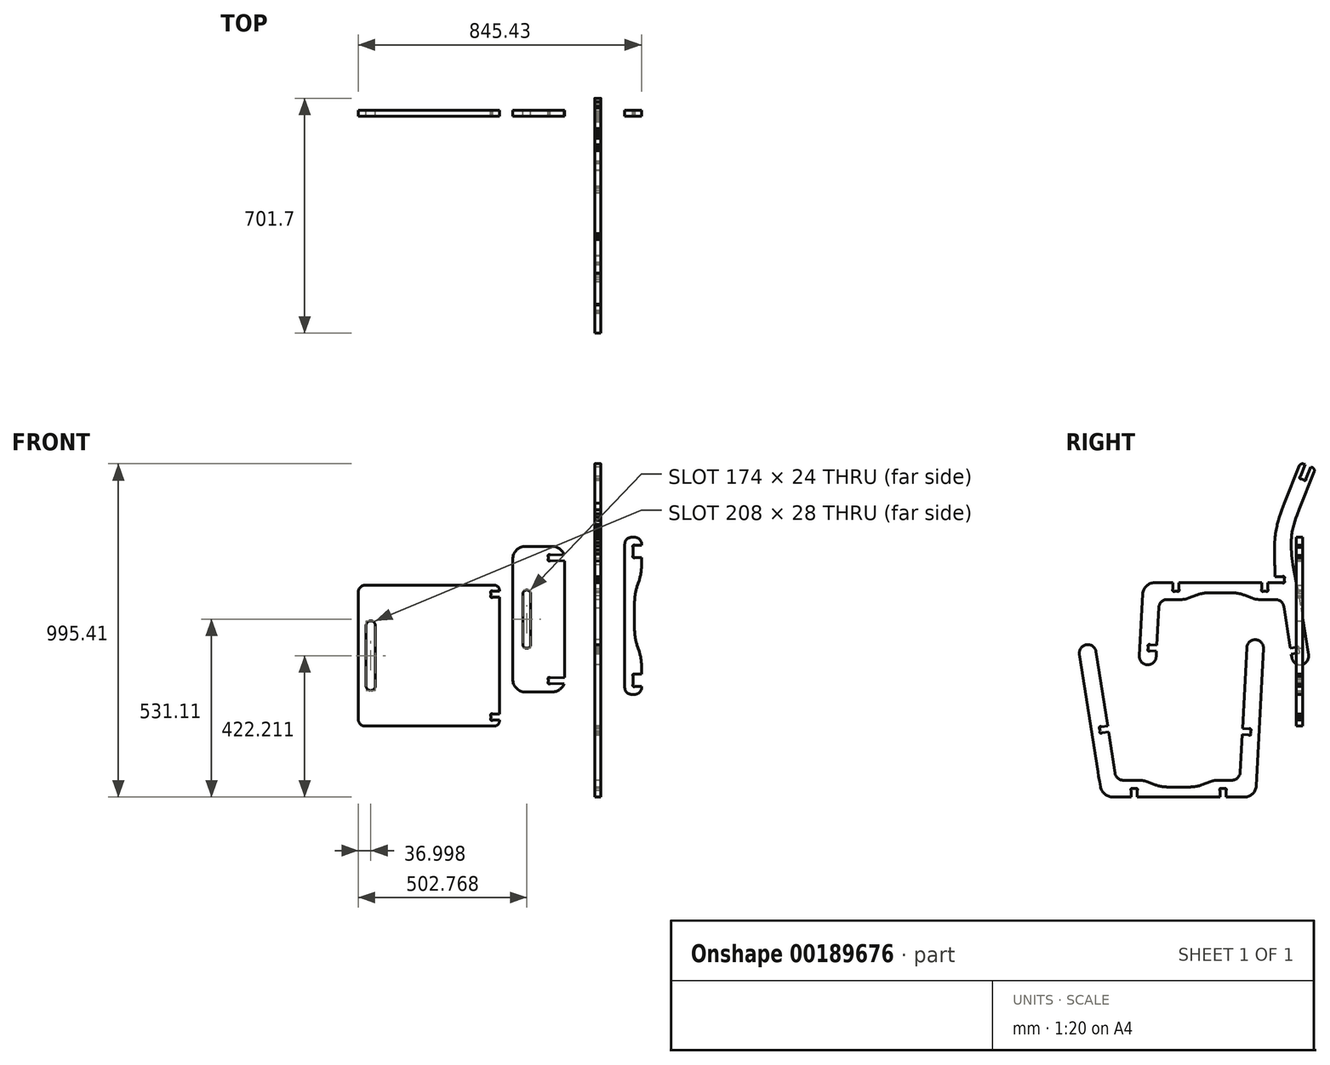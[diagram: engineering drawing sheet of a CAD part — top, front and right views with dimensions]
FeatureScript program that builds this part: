
annotation { "Feature Type Name" : "Feature", "Feature Type Description" : "" }
export const myFeature = defineFeature(function(context is Context, id is Id, definition is map)
    precondition{}
    {
        {
            assignVariable(context, id + "F0", {"name" : "ply", "anyValue" : 18});
        }
        {
            var Q0;
            Q0=qCreatedBy(makeId("Right.planeOp"),FACE);
            var sketch = newSketch(context, id + "F1", { "sketchPlane" : qUnion([Q0])});
            skLineSegment(sketch, "E0", {"start": v(-83.27, 173.83) * mm, "end": v(-83.93, 195.93) * mm});
            skLineSegment(sketch, "E1", {"start": v(-83.93, 195.93) * mm, "end": v(-83.96, 207) * mm});
            skLineSegment(sketch, "E2", {"start": v(-83.96, 207) * mm, "end": v(-83.75, 218.07) * mm});
            skLineSegment(sketch, "E3", {"start": v(-83.75, 218.07) * mm, "end": v(-83.24, 229.12) * mm});
            skLineSegment(sketch, "E4", {"start": v(-83.24, 229.12) * mm, "end": v(-82.4, 240.14) * mm});
            skLineSegment(sketch, "E5", {"start": v(-82.4, 240.14) * mm, "end": v(-81.86, 245.63) * mm});
            skLineSegment(sketch, "E6", {"start": v(-81.86, 245.63) * mm, "end": v(-81.2, 251.1) * mm});
            skLineSegment(sketch, "E7", {"start": v(-81.2, 251.1) * mm, "end": v(-80.46, 256.57) * mm});
            skLineSegment(sketch, "E8", {"start": v(-80.46, 256.57) * mm, "end": v(-79.6, 262.02) * mm});
            skLineSegment(sketch, "E9", {"start": v(-79.6, 262.02) * mm, "end": v(-78.64, 267.44) * mm});
            skLineSegment(sketch, "E10", {"start": v(-78.64, 267.44) * mm, "end": v(-77.57, 272.85) * mm});
            skLineSegment(sketch, "E11", {"start": v(-77.57, 272.85) * mm, "end": v(-76.4, 278.24) * mm});
            skLineSegment(sketch, "E12", {"start": v(-76.4, 278.24) * mm, "end": v(-75.13, 283.61) * mm});
            skLineSegment(sketch, "E13", {"start": v(-75.13, 283.61) * mm, "end": v(-72.33, 294.3) * mm});
            skLineSegment(sketch, "E14", {"start": v(-72.33, 294.3) * mm, "end": v(-69.21, 304.9) * mm});
            skLineSegment(sketch, "E15", {"start": v(-69.21, 304.9) * mm, "end": v(-65.8, 315.43) * mm});
            skLineSegment(sketch, "E16", {"start": v(-65.8, 315.43) * mm, "end": v(-62.16, 325.88) * mm});
            skLineSegment(sketch, "E17", {"start": v(-62.16, 325.88) * mm, "end": v(-54.3, 346.54) * mm});
            skLineSegment(sketch, "E18", {"start": v(-54.3, 346.54) * mm, "end": v(-9.72, 458.01) * mm});
            skArc(sketch, "E19", {"start": v(-9.72, 458.01) * mm, "mid": v(-4.37, 463.5) * mm, "end": v(3.28, 463.59) * mm});
            skLineSegment(sketch, "E20", {"start": v(3.28, 463.59) * mm, "end": v(7.92, 461.73) * mm});
            skLineSegment(sketch, "E21", {"start": v(7.92, 461.73) * mm, "end": v(-6.2, 426.41) * mm});
            skArc(sketch, "E22", {"start": v(-6.2, 426.41) * mm, "mid": v(-8.3, 421.16) * mm, "end": v(-3.05, 419.06) * mm});
            skLineSegment(sketch, "E23", {"start": v(-3.05, 419.06) * mm, "end": v(3.16, 416.58) * mm});
            skArc(sketch, "E24", {"start": v(3.16, 416.58) * mm, "mid": v(8.41, 414.48) * mm, "end": v(10.51, 419.73) * mm});
            skLineSegment(sketch, "E25", {"start": v(10.51, 419.73) * mm, "end": v(24.64, 455.04) * mm});
            skLineSegment(sketch, "E26", {"start": v(24.64, 455.04) * mm, "end": v(29.28, 453.19) * mm});
            skArc(sketch, "E27", {"start": v(29.28, 453.19) * mm, "mid": v(34.76, 447.84) * mm, "end": v(34.85, 440.19) * mm});
            skLineSegment(sketch, "E28", {"start": v(34.85, 440.19) * mm, "end": v(-9.74, 328.71) * mm});
            skLineSegment(sketch, "E29", {"start": v(-9.74, 328.71) * mm, "end": v(-16.51, 311.1) * mm});
            skLineSegment(sketch, "E30", {"start": v(-16.51, 311.1) * mm, "end": v(-19.69, 302.2) * mm});
            skLineSegment(sketch, "E31", {"start": v(-19.69, 302.2) * mm, "end": v(-22.66, 293.24) * mm});
            skLineSegment(sketch, "E32", {"start": v(-22.66, 293.24) * mm, "end": v(-25.37, 284.2) * mm});
            skLineSegment(sketch, "E33", {"start": v(-25.37, 284.2) * mm, "end": v(-26.61, 279.66) * mm});
            skLineSegment(sketch, "E34", {"start": v(-26.61, 279.66) * mm, "end": v(-27.77, 275.1) * mm});
            skLineSegment(sketch, "E35", {"start": v(-27.77, 275.1) * mm, "end": v(-28.85, 270.53) * mm});
            skLineSegment(sketch, "E36", {"start": v(-28.85, 270.53) * mm, "end": v(-29.83, 265.93) * mm});
            skLineSegment(sketch, "E37", {"start": v(-29.83, 265.93) * mm, "end": v(-30.7, 261.32) * mm});
            skLineSegment(sketch, "E38", {"start": v(-30.7, 261.32) * mm, "end": v(-31.48, 256.7) * mm});
            skLineSegment(sketch, "E39", {"start": v(-31.48, 256.7) * mm, "end": v(-32.14, 252.05) * mm});
            skLineSegment(sketch, "E40", {"start": v(-32.14, 252.05) * mm, "end": v(-32.69, 247.4) * mm});
            skLineSegment(sketch, "E41", {"start": v(-32.69, 247.4) * mm, "end": v(-33.13, 242.72) * mm});
            skLineSegment(sketch, "E42", {"start": v(-33.13, 242.72) * mm, "end": v(-33.48, 238.04) * mm});
            skLineSegment(sketch, "E43", {"start": v(-33.48, 238.04) * mm, "end": v(-33.72, 233.34) * mm});
            skLineSegment(sketch, "E44", {"start": v(-33.72, 233.34) * mm, "end": v(-33.88, 228.64) * mm});
            skLineSegment(sketch, "E45", {"start": v(-33.88, 228.64) * mm, "end": v(-33.94, 223.93) * mm});
            skLineSegment(sketch, "E46", {"start": v(-33.94, 223.93) * mm, "end": v(-33.92, 219.21) * mm});
            skLineSegment(sketch, "E47", {"start": v(-33.92, 219.21) * mm, "end": v(-33.63, 209.78) * mm});
            skLineSegment(sketch, "E48", {"start": v(-33.63, 209.78) * mm, "end": v(-33.04, 200.34) * mm});
            skLineSegment(sketch, "E49", {"start": v(-33.04, 200.34) * mm, "end": v(-32.18, 190.92) * mm});
            skLineSegment(sketch, "E50", {"start": v(-32.18, 190.92) * mm, "end": v(-31.1, 181.53) * mm});
            skLineSegment(sketch, "E51", {"start": v(-31.1, 181.53) * mm, "end": v(-29.8, 172.18) * mm});
            skLineSegment(sketch, "E52", {"start": v(-29.8, 172.18) * mm, "end": v(-28.33, 162.86) * mm});
            skLineSegment(sketch, "E53", {"start": v(-28.33, 162.86) * mm, "end": v(-10.62, 70.3) * mm});
            skLineSegment(sketch, "E54", {"start": v(-10.62, 70.3) * mm, "end": v(-4.36, 33.1) * mm});
            skLineSegment(sketch, "E55", {"start": v(-4.36, 33.1) * mm, "end": v(17.66, -107.27) * mm});
            skArc(sketch, "E56", {"start": v(17.66, -107.27) * mm, "mid": v(-3.16, -135.84) * mm, "end": v(-31.73, -115.02) * mm});
            skLineSegment(sketch, "E57", {"start": v(-31.73, -115.02) * mm, "end": v(-33.46, -104) * mm});
            skLineSegment(sketch, "E58", {"start": v(-33.46, -104) * mm, "end": v(-14.35, -101) * mm});
            skArc(sketch, "E59", {"start": v(-14.35, -101) * mm, "mid": v(-8.76, -100.13) * mm, "end": v(-9.64, -94.54) * mm});
            skLineSegment(sketch, "E60", {"start": v(-9.64, -94.54) * mm, "end": v(-10.68, -87.93) * mm});
            skArc(sketch, "E61", {"start": v(-10.68, -87.93) * mm, "mid": v(-11.55, -82.35) * mm, "end": v(-17.14, -83.22) * mm});
            skLineSegment(sketch, "E62", {"start": v(-17.14, -83.22) * mm, "end": v(-36.25, -86.22) * mm});
            skLineSegment(sketch, "E63", {"start": v(-36.25, -86.22) * mm, "end": v(-55.7, 37.73) * mm});
            skArc(sketch, "E64", {"start": v(-55.7, 37.73) * mm, "mid": v(-64.15, 52.85) * mm, "end": v(-80.4, 58.86) * mm});
            skLineSegment(sketch, "E65", {"start": v(-80.4, 58.86) * mm, "end": v(-128.9, 58.86) * mm});
            skArc(sketch, "E66", {"start": v(-128.9, 58.86) * mm, "mid": v(-139.97, 59.88) * mm, "end": v(-150.65, 62.94) * mm});
            skLineSegment(sketch, "E67", {"start": v(-150.65, 62.94) * mm, "end": v(-174.1, 72.06) * mm});
            skArc(sketch, "E68", {"start": v(-174.1, 72.06) * mm, "mid": v(-191.91, 77.14) * mm, "end": v(-210.35, 78.86) * mm});
            skLineSegment(sketch, "E69", {"start": v(-210.35, 78.86) * mm, "end": v(-279.97, 78.86) * mm});
            skArc(sketch, "E70", {"start": v(-279.97, 78.86) * mm, "mid": v(-298.41, 77.14) * mm, "end": v(-316.22, 72.06) * mm});
            skLineSegment(sketch, "E71", {"start": v(-316.22, 72.06) * mm, "end": v(-339.67, 62.94) * mm});
            skArc(sketch, "E72", {"start": v(-339.67, 62.94) * mm, "mid": v(-350.35, 59.88) * mm, "end": v(-361.42, 58.86) * mm});
            skLineSegment(sketch, "E73", {"start": v(-361.42, 58.86) * mm, "end": v(-404.15, 58.86) * mm});
            skArc(sketch, "E74", {"start": v(-404.15, 58.86) * mm, "mid": v(-421.35, 52) * mm, "end": v(-429.12, 35.18) * mm});
            skLineSegment(sketch, "E75", {"start": v(-429.12, 35.18) * mm, "end": v(-435.09, -77.5) * mm});
            skLineSegment(sketch, "E76", {"start": v(-435.09, -77.5) * mm, "end": v(-454.4, -76.47) * mm});
            skArc(sketch, "E77", {"start": v(-454.4, -76.47) * mm, "mid": v(-460.05, -76.17) * mm, "end": v(-460.35, -81.82) * mm});
            skLineSegment(sketch, "E78", {"start": v(-460.35, -81.82) * mm, "end": v(-460.7, -88.5) * mm});
            skArc(sketch, "E79", {"start": v(-460.7, -88.5) * mm, "mid": v(-461, -94.14) * mm, "end": v(-455.36, -94.44) * mm});
            skLineSegment(sketch, "E80", {"start": v(-455.36, -94.44) * mm, "end": v(-436.04, -95.47) * mm});
            skLineSegment(sketch, "E81", {"start": v(-436.04, -95.47) * mm, "end": v(-436.94, -112.47) * mm});
            skArc(sketch, "E82", {"start": v(-436.94, -112.47) * mm, "mid": v(-463.23, -136.1) * mm, "end": v(-486.87, -109.82) * mm});
            skLineSegment(sketch, "E83", {"start": v(-486.87, -109.82) * mm, "end": v(-477.04, 75.7) * mm});
            skArc(sketch, "E84", {"start": v(-477.04, 75.7) * mm, "mid": v(-466.17, 99.25) * mm, "end": v(-442.09, 108.86) * mm});
            skLineSegment(sketch, "E85", {"start": v(-442.09, 108.86) * mm, "end": v(-386.75, 108.86) * mm});
            skLineSegment(sketch, "E86", {"start": v(-386.75, 108.86) * mm, "end": v(-386.75, 89.51) * mm});
            skArc(sketch, "E87", {"start": v(-386.75, 89.51) * mm, "mid": v(-386.75, 83.86) * mm, "end": v(-381.1, 83.86) * mm});
            skLineSegment(sketch, "E88", {"start": v(-381.1, 83.86) * mm, "end": v(-374.4, 83.86) * mm});
            skArc(sketch, "E89", {"start": v(-374.4, 83.86) * mm, "mid": v(-368.75, 83.86) * mm, "end": v(-368.75, 89.51) * mm});
            skLineSegment(sketch, "E90", {"start": v(-368.75, 89.51) * mm, "end": v(-368.75, 108.86) * mm});
            skLineSegment(sketch, "E91", {"start": v(-368.75, 108.86) * mm, "end": v(-121.57, 108.86) * mm});
            skLineSegment(sketch, "E92", {"start": v(-121.57, 108.86) * mm, "end": v(-121.57, 89.51) * mm});
            skArc(sketch, "E93", {"start": v(-121.57, 89.51) * mm, "mid": v(-121.57, 83.86) * mm, "end": v(-115.92, 83.86) * mm});
            skLineSegment(sketch, "E94", {"start": v(-115.92, 83.86) * mm, "end": v(-109.23, 83.86) * mm});
            skArc(sketch, "E95", {"start": v(-109.23, 83.86) * mm, "mid": v(-103.57, 83.86) * mm, "end": v(-103.57, 89.51) * mm});
            skLineSegment(sketch, "E96", {"start": v(-103.57, 89.51) * mm, "end": v(-103.57, 108.86) * mm});
            skLineSegment(sketch, "E97", {"start": v(-103.57, 108.86) * mm, "end": v(-60.18, 108.86) * mm});
            skArc(sketch, "E98", {"start": v(-60.18, 108.86) * mm, "mid": v(-54.52, 108.86) * mm, "end": v(-54.52, 114.51) * mm});
            skLineSegment(sketch, "E99", {"start": v(-54.52, 114.51) * mm, "end": v(-54.52, 121.2) * mm});
            skArc(sketch, "E100", {"start": v(-54.52, 121.2) * mm, "mid": v(-54.52, 126.86) * mm, "end": v(-60.18, 126.86) * mm});
            skLineSegment(sketch, "E101", {"start": v(-60.18, 126.86) * mm, "end": v(-81.89, 126.86) * mm});
            skArc(sketch, "E102", {"start": v(-81.89, 126.86) * mm, "mid": v(-82.36, 150.35) * mm, "end": v(-83.27, 173.83) * mm});
            skSolve(sketch);
        }
        {
            var Q0;
            Q0 = qSketchRegion(id + "F1", true);
            extrude(context, id + "F2", {"entities" : qUnion([Q0]), "depth" : (getVariable(context, 'ply')) * mm});
        }
        {
            var Q0;
            Q0=qCreatedBy(makeId("Right.planeOp"),FACE);
            var sketch = newSketch(context, id + "F3", { "sketchPlane" : qUnion([Q0])});
            skArc(sketch, "E103", {"start": v(-211.02, -481.11) * mm, "mid": v(-193.81, -474.25) * mm, "end": v(-186.05, -457.44) * mm});
            skLineSegment(sketch, "E104", {"start": v(-186.05, -457.44) * mm, "end": v(-180.08, -344.77) * mm});
            skLineSegment(sketch, "E105", {"start": v(-180.08, -344.77) * mm, "end": v(-160.76, -345.8) * mm});
            skArc(sketch, "E106", {"start": v(-160.76, -345.8) * mm, "mid": v(-155.11, -346.09) * mm, "end": v(-154.81, -340.44) * mm});
            skLineSegment(sketch, "E107", {"start": v(-154.81, -340.44) * mm, "end": v(-154.48, -334.06) * mm});
            skArc(sketch, "E108", {"start": v(-154.48, -334.06) * mm, "mid": v(-153.88, -328.43) * mm, "end": v(-159.5, -327.83) * mm});
            skLineSegment(sketch, "E109", {"start": v(-159.5, -327.83) * mm, "end": v(-179.13, -326.8) * mm});
            skLineSegment(sketch, "E110", {"start": v(-179.13, -326.8) * mm, "end": v(-166.3, -84.76) * mm});
            skArc(sketch, "E111", {"start": v(-166.3, -84.76) * mm, "mid": v(-140, -61.11) * mm, "end": v(-116.37, -87.4) * mm});
            skLineSegment(sketch, "E112", {"start": v(-116.37, -87.4) * mm, "end": v(-138.13, -497.97) * mm});
            skArc(sketch, "E113", {"start": v(-138.13, -497.97) * mm, "mid": v(-149, -521.5) * mm, "end": v(-173.08, -531.11) * mm});
            skLineSegment(sketch, "E114", {"start": v(-173.08, -531.11) * mm, "end": v(-228.42, -531.11) * mm});
            skLineSegment(sketch, "E115", {"start": v(-228.42, -531.11) * mm, "end": v(-228.42, -511.77) * mm});
            skArc(sketch, "E116", {"start": v(-228.42, -511.77) * mm, "mid": v(-228.42, -506.11) * mm, "end": v(-234.08, -506.11) * mm});
            skLineSegment(sketch, "E117", {"start": v(-234.08, -506.11) * mm, "end": v(-240.76, -506.11) * mm});
            skArc(sketch, "E118", {"start": v(-240.76, -506.11) * mm, "mid": v(-246.42, -506.11) * mm, "end": v(-246.42, -511.77) * mm});
            skLineSegment(sketch, "E119", {"start": v(-246.42, -511.77) * mm, "end": v(-246.42, -531.11) * mm});
            skLineSegment(sketch, "E120", {"start": v(-246.42, -531.11) * mm, "end": v(-493.6, -531.11) * mm});
            skLineSegment(sketch, "E121", {"start": v(-493.6, -531.11) * mm, "end": v(-493.6, -511.77) * mm});
            skArc(sketch, "E122", {"start": v(-493.6, -511.77) * mm, "mid": v(-493.6, -506.11) * mm, "end": v(-499.25, -506.11) * mm});
            skLineSegment(sketch, "E123", {"start": v(-499.25, -506.11) * mm, "end": v(-505.94, -506.11) * mm});
            skArc(sketch, "E124", {"start": v(-505.94, -506.11) * mm, "mid": v(-511.6, -506.11) * mm, "end": v(-511.6, -511.77) * mm});
            skLineSegment(sketch, "E125", {"start": v(-511.6, -511.77) * mm, "end": v(-511.6, -531.11) * mm});
            skLineSegment(sketch, "E126", {"start": v(-511.6, -531.11) * mm, "end": v(-565.95, -531.11) * mm});
            skArc(sketch, "E127", {"start": v(-565.95, -531.11) * mm, "mid": v(-590.26, -522.32) * mm, "end": v(-603.32, -500) * mm});
            skLineSegment(sketch, "E128", {"start": v(-603.32, -500) * mm, "end": v(-604.68, -492.5) * mm});
            skLineSegment(sketch, "E129", {"start": v(-604.68, -492.5) * mm, "end": v(-605.99, -485.03) * mm});
            skLineSegment(sketch, "E130", {"start": v(-605.99, -485.03) * mm, "end": v(-607.65, -475.1) * mm});
            skLineSegment(sketch, "E131", {"start": v(-607.65, -475.1) * mm, "end": v(-608.72, -468.52) * mm});
            skLineSegment(sketch, "E132", {"start": v(-608.72, -468.52) * mm, "end": v(-610.8, -455.37) * mm});
            skLineSegment(sketch, "E133", {"start": v(-610.8, -455.37) * mm, "end": v(-665.83, -104.69) * mm});
            skArc(sketch, "E134", {"start": v(-665.83, -104.69) * mm, "mid": v(-645, -76.11) * mm, "end": v(-616.43, -96.94) * mm});
            skLineSegment(sketch, "E135", {"start": v(-616.43, -96.94) * mm, "end": v(-581.7, -318.25) * mm});
            skLineSegment(sketch, "E136", {"start": v(-581.7, -318.25) * mm, "end": v(-600.82, -321.25) * mm});
            skArc(sketch, "E137", {"start": v(-600.82, -321.25) * mm, "mid": v(-606.4, -322.13) * mm, "end": v(-605.53, -327.72) * mm});
            skLineSegment(sketch, "E138", {"start": v(-605.53, -327.72) * mm, "end": v(-604.5, -334.32) * mm});
            skArc(sketch, "E139", {"start": v(-604.5, -334.32) * mm, "mid": v(-603.61, -339.91) * mm, "end": v(-598.03, -339.04) * mm});
            skLineSegment(sketch, "E140", {"start": v(-598.03, -339.04) * mm, "end": v(-578.92, -336.04) * mm});
            skLineSegment(sketch, "E141", {"start": v(-578.92, -336.04) * mm, "end": v(-559.47, -459.99) * mm});
            skArc(sketch, "E142", {"start": v(-559.47, -459.99) * mm, "mid": v(-551.02, -475.11) * mm, "end": v(-534.77, -481.11) * mm});
            skLineSegment(sketch, "E143", {"start": v(-534.77, -481.11) * mm, "end": v(-486.26, -481.11) * mm});
            skArc(sketch, "E144", {"start": v(-486.26, -481.11) * mm, "mid": v(-475.2, -482.14) * mm, "end": v(-464.52, -485.2) * mm});
            skLineSegment(sketch, "E145", {"start": v(-464.52, -485.2) * mm, "end": v(-441.06, -494.31) * mm});
            skArc(sketch, "E146", {"start": v(-441.06, -494.31) * mm, "mid": v(-423.26, -499.4) * mm, "end": v(-404.82, -501.11) * mm});
            skLineSegment(sketch, "E147", {"start": v(-404.82, -501.11) * mm, "end": v(-335.2, -501.11) * mm});
            skArc(sketch, "E148", {"start": v(-335.2, -501.11) * mm, "mid": v(-316.76, -499.4) * mm, "end": v(-298.95, -494.31) * mm});
            skLineSegment(sketch, "E149", {"start": v(-298.95, -494.31) * mm, "end": v(-275.5, -485.2) * mm});
            skArc(sketch, "E150", {"start": v(-275.5, -485.2) * mm, "mid": v(-264.81, -482.14) * mm, "end": v(-253.75, -481.11) * mm});
            skLineSegment(sketch, "E151", {"start": v(-253.75, -481.11) * mm, "end": v(-211.02, -481.11) * mm});
            skSolve(sketch);
        }
        {
            var Q0;
            Q0 = qSketchRegion(id + "F3", true);
            extrude(context, id + "F4", {"entities" : qUnion([Q0]), "depth" : (getVariable(context, 'ply')) * mm});
        }
        {
            var Q0;
            Q0=qCreatedBy(makeId("Front.planeOp"),FACE);
            var sketch = newSketch(context, id + "F5", { "sketchPlane" : qUnion([Q0])});
            skLineSegment(sketch, "E152", {"start": v(-91.65, -192.5) * mm, "end": v(-133.1, -192.3) * mm});
            skArc(sketch, "E153", {"start": v(-133.1, -192.3) * mm, "mid": v(-138.75, -192.3) * mm, "end": v(-138.75, -186.64) * mm});
            skLineSegment(sketch, "E154", {"start": v(-138.75, -186.64) * mm, "end": v(-138.75, -180.36) * mm});
            skArc(sketch, "E155", {"start": v(-138.75, -180.36) * mm, "mid": v(-138.75, -174.7) * mm, "end": v(-133.1, -174.7) * mm});
            skLineSegment(sketch, "E156", {"start": v(-133.1, -174.7) * mm, "end": v(-89.36, -174.5) * mm});
            skLineSegment(sketch, "E157", {"start": v(-89.36, -174.5) * mm, "end": v(-89.36, 174.5) * mm});
            skLineSegment(sketch, "E158", {"start": v(-89.36, 174.5) * mm, "end": v(-133.1, 174.7) * mm});
            skArc(sketch, "E159", {"start": v(-133.1, 174.7) * mm, "mid": v(-138.75, 174.7) * mm, "end": v(-138.75, 180.36) * mm});
            skLineSegment(sketch, "E160", {"start": v(-138.75, 180.36) * mm, "end": v(-138.75, 186.64) * mm});
            skArc(sketch, "E161", {"start": v(-138.75, 186.64) * mm, "mid": v(-138.75, 192.3) * mm, "end": v(-133.1, 192.3) * mm});
            skLineSegment(sketch, "E162", {"start": v(-133.1, 192.3) * mm, "end": v(-91.65, 192.5) * mm});
            skArc(sketch, "E163", {"start": v(-91.65, 192.5) * mm, "mid": v(-105.56, 210.63) * mm, "end": v(-127.36, 217.5) * mm});
            skLineSegment(sketch, "E164", {"start": v(-127.36, 217.5) * mm, "end": v(-206.94, 217.5) * mm});
            skArc(sketch, "E165", {"start": v(-206.94, 217.5) * mm, "mid": v(-233.81, 206.37) * mm, "end": v(-244.94, 179.5) * mm});
            skLineSegment(sketch, "E166", {"start": v(-244.94, 179.5) * mm, "end": v(-244.94, -179.5) * mm});
            skArc(sketch, "E167", {"start": v(-244.94, -179.5) * mm, "mid": v(-233.81, -206.37) * mm, "end": v(-206.94, -217.5) * mm});
            skLineSegment(sketch, "E168", {"start": v(-206.94, -217.5) * mm, "end": v(-127.36, -217.5) * mm});
            skArc(sketch, "E169", {"start": v(-127.36, -217.5) * mm, "mid": v(-105.56, -210.63) * mm, "end": v(-91.65, -192.5) * mm});
            skArc(sketch, "E170", {"start": v(-214.94, -75) * mm, "mid": v(-202.94, -87) * mm, "end": v(-190.94, -75) * mm});
            skLineSegment(sketch, "E171", {"start": v(-190.94, -75) * mm, "end": v(-190.94, 75) * mm});
            skArc(sketch, "E172", {"start": v(-190.94, 75) * mm, "mid": v(-202.94, 87) * mm, "end": v(-214.94, 75) * mm});
            skLineSegment(sketch, "E173", {"start": v(-214.94, 75) * mm, "end": v(-214.94, -75) * mm});
            skSolve(sketch);
        }
        {
            var Q0;
            Q0 = qSketchRegion(id + "F5", true);
            extrude(context, id + "F6", {"entities" : qUnion([Q0]), "depth" : (getVariable(context, 'ply')) * mm});
        }
        {
            var Q0;
            Q0=qCreatedBy(makeId("Front.planeOp"),FACE);
            var sketch = newSketch(context, id + "F7", { "sketchPlane" : qUnion([Q0])});
            skLineSegment(sketch, "E174", {"start": v(119.72, -224.5) * mm, "end": v(109.72, -224.5) * mm});
            skArc(sketch, "E175", {"start": v(109.72, -224.5) * mm, "mid": v(95.58, -218.64) * mm, "end": v(89.72, -204.5) * mm});
            skLineSegment(sketch, "E176", {"start": v(89.72, -204.5) * mm, "end": v(89.72, 224.5) * mm});
            skArc(sketch, "E177", {"start": v(89.72, 224.5) * mm, "mid": v(95.58, 238.65) * mm, "end": v(109.72, 244.5) * mm});
            skLineSegment(sketch, "E178", {"start": v(109.72, 244.5) * mm, "end": v(119.72, 244.5) * mm});
            skArc(sketch, "E179", {"start": v(119.72, 244.5) * mm, "mid": v(133.86, 238.65) * mm, "end": v(139.72, 224.5) * mm});
            skLineSegment(sketch, "E180", {"start": v(139.72, 224.5) * mm, "end": v(139.72, 220.5) * mm});
            skLineSegment(sketch, "E181", {"start": v(139.72, 220.5) * mm, "end": v(120.37, 220.5) * mm});
            skArc(sketch, "E182", {"start": v(120.37, 220.5) * mm, "mid": v(114.72, 220.5) * mm, "end": v(114.72, 214.85) * mm});
            skLineSegment(sketch, "E183", {"start": v(114.72, 214.85) * mm, "end": v(114.72, 190.16) * mm});
            skArc(sketch, "E184", {"start": v(114.72, 190.16) * mm, "mid": v(114.72, 184.5) * mm, "end": v(120.37, 184.5) * mm});
            skLineSegment(sketch, "E185", {"start": v(120.37, 184.5) * mm, "end": v(139.72, 184.5) * mm});
            skLineSegment(sketch, "E186", {"start": v(139.72, 184.5) * mm, "end": v(139.72, 161.54) * mm});
            skArc(sketch, "E187", {"start": v(139.72, 161.54) * mm, "mid": v(137.81, 137.7) * mm, "end": v(132.14, 114.48) * mm});
            skLineSegment(sketch, "E188", {"start": v(132.14, 114.48) * mm, "end": v(126.5, 97.41) * mm});
            skArc(sketch, "E189", {"start": v(126.5, 97.41) * mm, "mid": v(120.84, 74.18) * mm, "end": v(118.93, 50.35) * mm});
            skLineSegment(sketch, "E190", {"start": v(118.93, 50.35) * mm, "end": v(118.93, -30.34) * mm});
            skArc(sketch, "E191", {"start": v(118.93, -30.34) * mm, "mid": v(120.84, -54.18) * mm, "end": v(126.5, -77.4) * mm});
            skLineSegment(sketch, "E192", {"start": v(126.5, -77.4) * mm, "end": v(132.14, -94.47) * mm});
            skArc(sketch, "E193", {"start": v(132.14, -94.47) * mm, "mid": v(137.81, -117.7) * mm, "end": v(139.72, -141.53) * mm});
            skLineSegment(sketch, "E194", {"start": v(139.72, -141.53) * mm, "end": v(139.72, -164.5) * mm});
            skLineSegment(sketch, "E195", {"start": v(139.72, -164.5) * mm, "end": v(120.37, -164.5) * mm});
            skArc(sketch, "E196", {"start": v(120.37, -164.5) * mm, "mid": v(114.72, -164.5) * mm, "end": v(114.72, -170.15) * mm});
            skLineSegment(sketch, "E197", {"start": v(114.72, -170.15) * mm, "end": v(114.72, -194.84) * mm});
            skArc(sketch, "E198", {"start": v(114.72, -194.84) * mm, "mid": v(114.72, -200.5) * mm, "end": v(120.37, -200.5) * mm});
            skLineSegment(sketch, "E199", {"start": v(120.37, -200.5) * mm, "end": v(139.72, -200.5) * mm});
            skLineSegment(sketch, "E200", {"start": v(139.72, -200.5) * mm, "end": v(139.72, -204.5) * mm});
            skArc(sketch, "E201", {"start": v(139.72, -204.5) * mm, "mid": v(133.86, -218.64) * mm, "end": v(119.72, -224.5) * mm});
            skSolve(sketch);
        }
        {
            var Q0;
            Q0 = qSketchRegion(id + "F7", true);
            extrude(context, id + "F8", {"entities" : qUnion([Q0]), "depth" : (getVariable(context, 'ply')) * mm});
        }
        {
            var Q0;
            Q0=qCreatedBy(makeId("Front.planeOp"),FACE);
            var sketch = newSketch(context, id + "F9", { "sketchPlane" : qUnion([Q0])});
            skLineSegment(sketch, "E202", {"start": v(-284.74, -304.4) * mm, "end": v(-284.74, -301.4) * mm});
            skLineSegment(sketch, "E203", {"start": v(-284.74, -301.4) * mm, "end": v(-304.52, -301.2) * mm});
            skArc(sketch, "E204", {"start": v(-304.52, -301.2) * mm, "mid": v(-310.18, -301.2) * mm, "end": v(-310.18, -295.54) * mm});
            skLineSegment(sketch, "E205", {"start": v(-310.18, -295.54) * mm, "end": v(-310.18, -289.26) * mm});
            skArc(sketch, "E206", {"start": v(-310.18, -289.26) * mm, "mid": v(-310.18, -283.6) * mm, "end": v(-304.52, -283.6) * mm});
            skLineSegment(sketch, "E207", {"start": v(-304.52, -283.6) * mm, "end": v(-284.74, -283.4) * mm});
            skLineSegment(sketch, "E208", {"start": v(-284.74, -283.4) * mm, "end": v(-284.74, 65.6) * mm});
            skLineSegment(sketch, "E209", {"start": v(-284.74, 65.6) * mm, "end": v(-304.52, 65.8) * mm});
            skArc(sketch, "E210", {"start": v(-304.52, 65.8) * mm, "mid": v(-310.18, 65.8) * mm, "end": v(-310.18, 71.46) * mm});
            skLineSegment(sketch, "E211", {"start": v(-310.18, 71.46) * mm, "end": v(-310.18, 77.74) * mm});
            skArc(sketch, "E212", {"start": v(-310.18, 77.74) * mm, "mid": v(-310.18, 83.4) * mm, "end": v(-304.52, 83.4) * mm});
            skLineSegment(sketch, "E213", {"start": v(-304.52, 83.4) * mm, "end": v(-284.74, 83.6) * mm});
            skLineSegment(sketch, "E214", {"start": v(-284.74, 83.6) * mm, "end": v(-284.74, 86.6) * mm});
            skArc(sketch, "E215", {"start": v(-284.74, 86.6) * mm, "mid": v(-289.13, 97.2) * mm, "end": v(-299.74, 101.6) * mm});
            skLineSegment(sketch, "E216", {"start": v(-299.74, 101.6) * mm, "end": v(-685.71, 101.6) * mm});
            skArc(sketch, "E217", {"start": v(-685.71, 101.6) * mm, "mid": v(-699.85, 95.74) * mm, "end": v(-705.71, 81.6) * mm});
            skLineSegment(sketch, "E218", {"start": v(-705.71, 81.6) * mm, "end": v(-705.71, -299.4) * mm});
            skArc(sketch, "E219", {"start": v(-705.71, -299.4) * mm, "mid": v(-699.85, -313.54) * mm, "end": v(-685.71, -319.4) * mm});
            skLineSegment(sketch, "E220", {"start": v(-685.71, -319.4) * mm, "end": v(-299.74, -319.4) * mm});
            skArc(sketch, "E221", {"start": v(-299.74, -319.4) * mm, "mid": v(-289.13, -315) * mm, "end": v(-284.74, -304.4) * mm});
            skArc(sketch, "E222", {"start": v(-682.71, -18.9) * mm, "mid": v(-668.71, -4.9) * mm, "end": v(-654.71, -18.9) * mm});
            skLineSegment(sketch, "E223", {"start": v(-654.71, -18.9) * mm, "end": v(-654.71, -198.9) * mm});
            skArc(sketch, "E224", {"start": v(-654.71, -198.9) * mm, "mid": v(-668.71, -212.9) * mm, "end": v(-682.71, -198.9) * mm});
            skLineSegment(sketch, "E225", {"start": v(-682.71, -198.9) * mm, "end": v(-682.71, -18.9) * mm});
            skSolve(sketch);
        }
        {
            var Q0;
            Q0 = qSketchRegion(id + "F9", true);
            extrude(context, id + "F10", {"entities" : qUnion([Q0]), "depth" : (getVariable(context, 'ply')) * mm});
        }
    });
